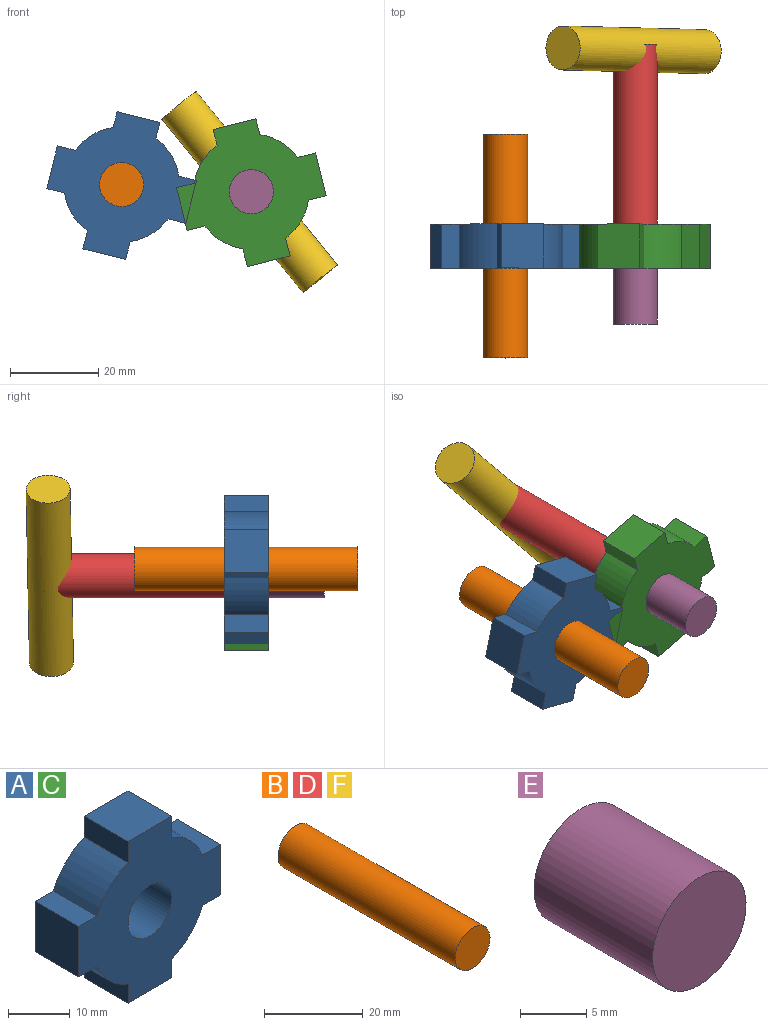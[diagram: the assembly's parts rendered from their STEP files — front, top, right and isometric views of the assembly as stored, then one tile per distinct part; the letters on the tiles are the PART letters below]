
ASSEMBLY  parts=6 mates=3
PART A: 19 faces, bbox 32.5x10x32.1 mm
  f0: plane 10x10mm, normal (1,0,0), area 100mm2, adj f1,f15,f17,f18
  f1: plane 10x4.17mm, normal (0,0,1), area 41.7mm2, adj f0,f2,f17,f18
  f2: cylinder r=13.1mm len=10mm, axis (0,1,0), area 103.2mm2, adj f1,f3,f17,f18
  f3: plane 10x4.17mm, normal (1,0,0), area 41.7mm2, adj f2,f4,f17,f18
  f4: plane 10x10mm, normal (0,0,1), area 100mm2, adj f3,f5,f17,f18
  f5: plane 10x4.17mm, normal (-1,0,0), area 41.7mm2, adj f4,f6,f17,f18
  f6: cylinder r=13.1mm len=10mm, axis (0,1,0), area 103.2mm2, adj f5,f7,f17,f18
  f7: plane 10x4.17mm, normal (0,0,1), area 41.7mm2, adj f6,f8,f17,f18
  f8: plane 10x10mm, normal (-1,0,0), area 100mm2, adj f7,f9,f17,f18
  f9: plane 10x4.17mm, normal (0,0,-1), area 41.7mm2, adj f8,f10,f17,f18
  f10: cylinder r=13.1mm len=10mm, axis (0,1,0), area 103.2mm2, adj f9,f11,f17,f18
  f11: plane 10x3.69mm, normal (-1,0,0), area 36.9mm2, adj f10,f12,f17,f18
  f12: plane 10x10mm, normal (0,0,-1), area 100mm2, adj f11,f13,f17,f18
  f13: plane 10x3.69mm, normal (1,0,0), area 36.9mm2, adj f12,f14,f17,f18
  f14: cylinder r=13.1mm len=10mm, axis (0,1,0), area 103.2mm2, adj f13,f15,f17,f18
  f15: plane 10x4.17mm, normal (0,0,-1), area 41.7mm2, adj f0,f14,f17,f18
  f16: cylinder r=5mm len=10mm, axis (0,1,0), area 314.2mm2, adj f17,f18
  f17: plane 32.55x32.08mm, normal (0,-1,0), area 595.8mm2, adj f0,f1,f2,f3,f4,f5,f6,f7
  f18: plane 32.55x32.08mm, normal (0,1,0), area 595.8mm2, adj f0,f1,f2,f3,f4,f5,f6,f7
PART B: 3 faces, bbox 10x50.8x10 mm
  f0: cylinder r=5mm len=50.8mm, axis (0,1,0), area 1595.9mm2, adj f1,f2
  f1: plane 10x10mm, normal (0,-1,0), area 78.5mm2, adj f0
  f2: plane 10x10mm, normal (0,1,0), area 78.5mm2, adj f0
PART C: same geometry as A
PART D: same geometry as B
PART E: 3 faces, bbox 10x12.7x10 mm
  f0: cylinder r=5mm len=12.7mm, axis (0,1,0), area 399mm2, adj f1,f2
  f1: plane 10x10mm, normal (0,-1,0), area 78.5mm2, adj f0
  f2: plane 10x10mm, normal (0,1,0), area 78.5mm2, adj f0
PART F: same geometry as B
PLACE A rot(axis=(0,-1,0),166deg) t=(-4.82,-4.76,1.83)mm
PLACE B t=(-42.94,15.64,-46.23)mm fixed
PLACE C rot(axis=(-0.99,0,-0.12),180deg) t=(24.63,-14.76,0.22)mm
PLACE D rot(axis=(0,1,0),166deg) t=(49.97,36.04,56.07)mm
PLACE E t=(-13.17,-14.76,40.21)mm fixed
PLACE F rot(axis=(0.86,-0.19,0.47),91.2deg) t=(-30.91,69.52,-12.6)mm
MATE revolute D.f0 <-> E.f0  axis (0,-1,0) through (24.63,-14.76,0.22)mm
MATE revolute A.f16 <-> B.f0  axis (0,1,0) through (-4.82,-9.76,1.83)mm
MATE fastened C.f16 <-> D.f0  axis (0,-1,0) through (24.63,-14.76,0.22)mm
